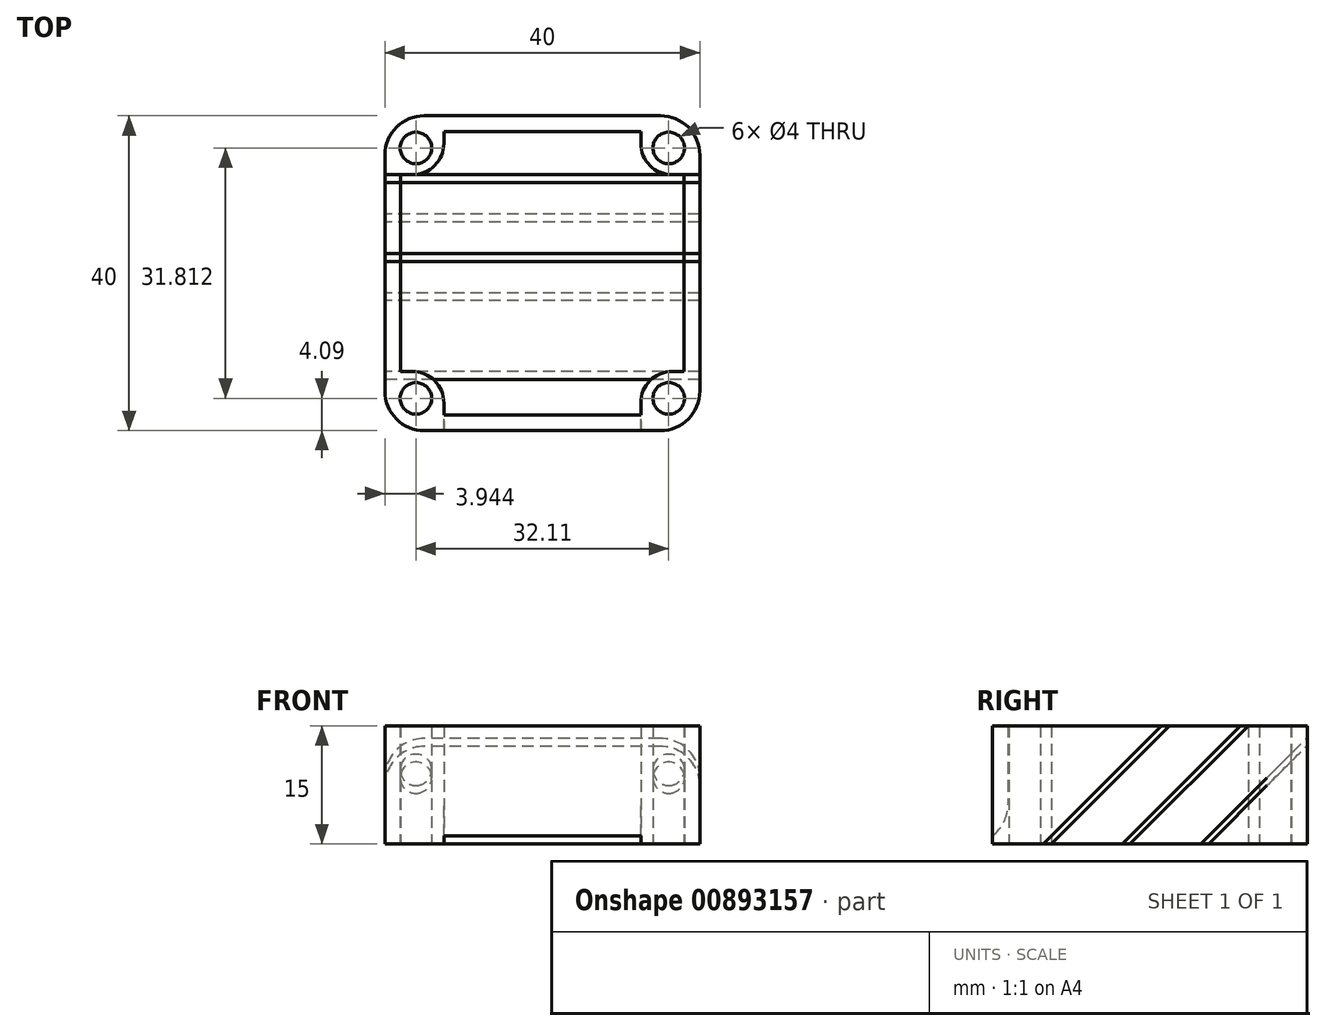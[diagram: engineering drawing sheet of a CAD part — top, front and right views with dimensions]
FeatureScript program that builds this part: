
annotation { "Feature Type Name" : "Feature", "Feature Type Description" : "" }
export const myFeature = defineFeature(function(context is Context, id is Id, definition is map)
    precondition{}
    {
        {
            var Q0;
            Q0=qCreatedBy(makeId("Top.planeOp"),FACE);
            var sketch = newSketch(context, id + "F0", { "sketchPlane" : qUnion([Q0])});
            skCircle(sketch, "E0", {"center": v(-57.98, 66.95) * mm, "radius": 2 * mm});
            skCircle(sketch, "E1", {"center": v(-25.87, 66.95) * mm, "radius": 2 * mm});
            skCircle(sketch, "E2", {"center": v(-25.87, 35.14) * mm, "radius": 2 * mm});
            skCircle(sketch, "E3", {"center": v(-57.98, 35.14) * mm, "radius": 2 * mm});
            skLineSegment(sketch, "E4.bottom", {"start": v(-21.92, 31.05) * mm, "end": v(-61.92, 31.05) * mm});
            skLineSegment(sketch, "E4.top", {"start": v(-21.92, 71.05) * mm, "end": v(-61.92, 71.05) * mm});
            skLineSegment(sketch, "E4.left", {"start": v(-21.92, 31.05) * mm, "end": v(-21.92, 71.05) * mm});
            skLineSegment(sketch, "E4.right", {"start": v(-61.92, 31.05) * mm, "end": v(-61.92, 71.05) * mm});
            skPoint(sketch, "E4.middle", {"position": v(-41.92, 51.05) * mm});
            skPoint(sketch, "E5", {"position": v(-61.92, 63.55) * mm});
            skPoint(sketch, "E6", {"position": v(-21.92, 63.55) * mm});
            skPoint(sketch, "E7", {"position": v(-61.92, 38.55) * mm});
            skPoint(sketch, "E8", {"position": v(-21.92, 38.55) * mm});
            skPoint(sketch, "E9", {"position": v(-54.42, 71.05) * mm});
            skPoint(sketch, "E10", {"position": v(-29.42, 71.05) * mm});
            skPoint(sketch, "E11", {"position": v(-29.42, 31.05) * mm});
            skPoint(sketch, "E12", {"position": v(-54.42, 31.05) * mm});
            skLineSegment(sketch, "E13", {"start": v(-61.92, 63.55) * mm, "end": v(-54.42, 63.55) * mm});
            skLineSegment(sketch, "E14", {"start": v(-54.42, 63.55) * mm, "end": v(-54.42, 71.05) * mm});
            skLineSegment(sketch, "E15", {"start": v(-29.42, 71.05) * mm, "end": v(-29.42, 63.55) * mm});
            skLineSegment(sketch, "E16", {"start": v(-29.42, 63.55) * mm, "end": v(-21.92, 63.55) * mm});
            skLineSegment(sketch, "E17", {"start": v(-61.92, 38.55) * mm, "end": v(-54.42, 38.55) * mm});
            skLineSegment(sketch, "E18", {"start": v(-54.42, 38.55) * mm, "end": v(-54.42, 31.05) * mm});
            skLineSegment(sketch, "E19", {"start": v(-21.92, 38.55) * mm, "end": v(-29.42, 38.55) * mm});
            skLineSegment(sketch, "E20", {"start": v(-29.42, 38.55) * mm, "end": v(-29.42, 31.05) * mm});
            skPoint(sketch, "E21", {"position": v(-59.92, 63.55) * mm});
            skPoint(sketch, "E22", {"position": v(-59.92, 38.55) * mm});
            skPoint(sketch, "E23", {"position": v(-54.42, 33.05) * mm});
            skPoint(sketch, "E24", {"position": v(-29.42, 33.05) * mm});
            skPoint(sketch, "E25", {"position": v(-23.92, 38.55) * mm});
            skPoint(sketch, "E26", {"position": v(-23.92, 63.55) * mm});
            skPoint(sketch, "E27", {"position": v(-29.42, 69.05) * mm});
            skPoint(sketch, "E28", {"position": v(-54.42, 69.05) * mm});
            skLineSegment(sketch, "E29", {"start": v(-59.92, 63.55) * mm, "end": v(-59.92, 38.55) * mm});
            skLineSegment(sketch, "E30", {"start": v(-54.42, 33.05) * mm, "end": v(-29.42, 33.05) * mm});
            skLineSegment(sketch, "E31", {"start": v(-23.92, 38.55) * mm, "end": v(-23.92, 63.55) * mm});
            skLineSegment(sketch, "E32", {"start": v(-29.42, 69.05) * mm, "end": v(-54.42, 69.05) * mm});
            skSolve(sketch);
        }
        {
            var Q0;
            Q0 = qSketchRegion(id + "F0", true);
            extrude(context, id + "F1", {"entities" : qUnion([Q0]), "depth" : 15 * mm, "offsetDistance" : 25 * mm});
        }
        {
            var Q0;
            Q0=makeQuery(id+"F1.opExtrude","SWEPT_EDGE",EDGE,{"disambiguationData":[OSD([sQuery(id+"F0.wireOp",EDGE,"E4.top"),sQuery(id+"F0.wireOp",EDGE,"E4.right")])]});
            var Q1;
            Q1=makeQuery(id+"F1.opExtrude","SWEPT_EDGE",EDGE,{"disambiguationData":[OSD([sQuery(id+"F0.wireOp",EDGE,"E4.bottom"),sQuery(id+"F0.wireOp",EDGE,"E4.right")])]});
            var Q2;
            Q2=makeQuery(id+"F1.opExtrude","SWEPT_EDGE",EDGE,{"disambiguationData":[OSD([sQuery(id+"F0.wireOp",EDGE,"E4.bottom"),sQuery(id+"F0.wireOp",EDGE,"E4.left")])]});
            var Q3;
            Q3=makeQuery(id+"F1.opExtrude","SWEPT_EDGE",EDGE,{"disambiguationData":[OSD([sQuery(id+"F0.wireOp",EDGE,"E4.top"),sQuery(id+"F0.wireOp",EDGE,"E4.left")])]});
            fillet(context, id + "F2", {"entities" : qUnion([Q0, Q1, Q2, Q3]), "radius" : 5 * mm, "tangentPropagation" : true, "allowEdgeOverflow" : false});
        }
        {
            var Q0;
            Q0=makeQuery(id+"F1.opExtrude","SWEPT_EDGE",EDGE,{"disambiguationData":[OSD([sQuery(id+"F0.wireOp",EDGE,"E13"),sQuery(id+"F0.wireOp",EDGE,"E14")])]});
            var Q1;
            Q1=makeQuery(id+"F1.opExtrude","SWEPT_EDGE",EDGE,{"disambiguationData":[OSD([sQuery(id+"F0.wireOp",EDGE,"E15"),sQuery(id+"F0.wireOp",EDGE,"E16")])]});
            var Q2;
            Q2=makeQuery(id+"F1.opExtrude","SWEPT_EDGE",EDGE,{"disambiguationData":[OSD([sQuery(id+"F0.wireOp",EDGE,"E19"),sQuery(id+"F0.wireOp",EDGE,"E20")])]});
            var Q3;
            Q3=makeQuery(id+"F1.opExtrude","SWEPT_EDGE",EDGE,{"disambiguationData":[OSD([sQuery(id+"F0.wireOp",EDGE,"E17"),sQuery(id+"F0.wireOp",EDGE,"E18")])]});
            fillet(context, id + "F3", {"entities" : qUnion([Q0, Q1, Q2, Q3]), "radius" : 4 * mm, "tangentPropagation" : true, "allowEdgeOverflow" : false});
        }
        {
            var Q0;
            Q0=makeQuery(id+"F1.opExtrude","SWEPT_FACE",FACE,{"disambiguationData":[OSD([sQuery(id+"F0.wireOp",EDGE,"E4.right")])]});
            var sketch = newSketch(context, id + "F4", { "sketchPlane" : qUnion([Q0])});
            skPoint(sketch, "E33", {"position": v(-66.05, 7.5) * mm});
            skPoint(sketch, "E34", {"position": v(-51.05, 0) * mm});
            skPoint(sketch, "E35", {"position": v(-58.55, 0) * mm});
            skPoint(sketch, "E36", {"position": v(-57.55, 0) * mm});
            skPoint(sketch, "E37", {"position": v(-66.05, 8.5) * mm});
            skLineSegment(sketch, "E38", {"start": v(-66.05, 7.5) * mm, "end": v(-58.55, 0) * mm});
            skLineSegment(sketch, "E39", {"start": v(-66.05, 8.5) * mm, "end": v(-57.55, 0) * mm});
            skLineSegment(sketch, "E40", {"start": v(-66.05, 7.5) * mm, "end": v(-66.05, 8.5) * mm});
            skLineSegment(sketch, "E41", {"start": v(-58.55, 0) * mm, "end": v(-57.55, 0) * mm});
            skLineSegment(sketch, "E42", {"start": v(-66.05, 8.5) * mm, "end": v(-66.05, 15) * mm});
            skLineSegment(sketch, "E43.1.0.0", {"start": v(-56.05, 7.5) * mm, "end": v(-48.55, 0) * mm});
            skLineSegment(sketch, "E43.1.0.1", {"start": v(-56.05, 8.5) * mm, "end": v(-47.55, 0) * mm});
            skLineSegment(sketch, "E43.1.0.2", {"start": v(-48.55, 0) * mm, "end": v(-47.55, 0) * mm});
            skLineSegment(sketch, "E43.2.0.0", {"start": v(-46.05, 7.5) * mm, "end": v(-38.55, 0) * mm});
            skLineSegment(sketch, "E43.2.0.1", {"start": v(-46.05, 8.5) * mm, "end": v(-37.55, 0) * mm});
            skLineSegment(sketch, "E43.2.0.2", {"start": v(-38.55, 0) * mm, "end": v(-37.55, 0) * mm});
            skLineSegment(sketch, "E43.direction1", {"start": v(-58.55, 0) * mm, "end": v(-48.55, 0) * mm, "construction": true});
            skLineSegment(sketch, "E44", {"start": v(-56.05, 7.5) * mm, "end": v(-63.55, 15) * mm});
            skLineSegment(sketch, "E45", {"start": v(-56.05, 8.5) * mm, "end": v(-62.55, 15) * mm});
            skLineSegment(sketch, "E46", {"start": v(-63.55, 15) * mm, "end": v(-62.55, 15) * mm});
            skLineSegment(sketch, "E47", {"start": v(-46.05, 7.5) * mm, "end": v(-53.55, 15) * mm});
            skLineSegment(sketch, "E48", {"start": v(-46.05, 8.5) * mm, "end": v(-52.55, 15) * mm});
            skLineSegment(sketch, "E49", {"start": v(-53.55, 15) * mm, "end": v(-52.55, 15) * mm});
            skLineSegment(sketch, "E50", {"start": v(-66.05, 7.5) * mm, "end": v(-70.94, 12.4) * mm});
            skLineSegment(sketch, "E51", {"start": v(-66.05, 8.5) * mm, "end": v(-70.94, 13.4) * mm});
            skLineSegment(sketch, "E52", {"start": v(-70.94, 13.4) * mm, "end": v(-70.94, 12.4) * mm});
            skLineSegment(sketch, "E53", {"start": v(-70.94, 13.4) * mm, "end": v(-66.05, 8.5) * mm});
            skLineSegment(sketch, "E54", {"start": v(-70.94, 12.4) * mm, "end": v(-66.05, 7.5) * mm});
            skSolve(sketch);
        }
        {
            var Q0;
            Q0 = qSketchRegion(id + "F4", true);
            extrude(context, id + "F5", {"entities" : qUnion([Q0]), "oppositeDirection" : true, "depth" : 40 * mm, "offsetDistance" : 25 * mm});
        }
        {
            var Q0;
            Q0=makeQuery(id+"F5.opExtrude","CAP_EDGE",EDGE,{"disambiguationData":[OSD([sQuery(id+"F4.wireOp",EDGE,"E52")])],"isStart":true});
            var Q1;
            Q1=makeQuery(id+"F5.opExtrude","CAP_EDGE",EDGE,{"disambiguationData":[OSD([sQuery(id+"F4.wireOp",EDGE,"E52")])],"isStart":false});
            fillet(context, id + "F6", {"entities" : qUnion([Q0, Q1]), "radius" : 5 * mm, "tangentPropagation" : true, "allowEdgeOverflow" : false});
        }
        {
            var Q0;
            Q0=makeQuery(id+"F1.opExtrude","CAP_FACE",FACE,{"disambiguationData":[OSD([sQuery(id+"F0.wireOp",EDGE,"E0"),sQuery(id+"F0.wireOp",EDGE,"E1"),sQuery(id+"F0.wireOp",EDGE,"E2"),sQuery(id+"F0.wireOp",EDGE,"E3"),sQuery(id+"F0.wireOp",EDGE,"E4.bottom"),sQuery(id+"F0.wireOp",EDGE,"E4.top"),sQuery(id+"F0.wireOp",EDGE,"E4.left"),sQuery(id+"F0.wireOp",EDGE,"E4.right"),sQuery(id+"F0.wireOp",EDGE,"E13"),sQuery(id+"F0.wireOp",EDGE,"E14"),sQuery(id+"F0.wireOp",EDGE,"E15"),sQuery(id+"F0.wireOp",EDGE,"E16"),sQuery(id+"F0.wireOp",EDGE,"E17"),sQuery(id+"F0.wireOp",EDGE,"E18"),sQuery(id+"F0.wireOp",EDGE,"E19"),sQuery(id+"F0.wireOp",EDGE,"E20"),sQuery(id+"F0.wireOp",EDGE,"E29"),sQuery(id+"F0.wireOp",EDGE,"E30"),sQuery(id+"F0.wireOp",EDGE,"E31"),sQuery(id+"F0.wireOp",EDGE,"E32")])],"isStart":true});
            var sketch = newSketch(context, id + "F7", { "sketchPlane" : qUnion([Q0])});
            skCircle(sketch, "E55", {"center": v(-25.87, -66.95) * mm, "radius": 2 * mm});
            skCircle(sketch, "E56", {"center": v(-57.98, -66.95) * mm, "radius": 2 * mm});
            skSolve(sketch);
        }
        {
            var Q0;
            Q0 = qSketchRegion(id + "F7", true);
            extrude(context, id + "F8", {"entities" : qUnion([Q0]), "operationType" : NewBodyOperationType.REMOVE, "oppositeDirection" : true, "depth" : 25 * mm, "offsetDistance" : 25 * mm});
        }
        {
            var Q0;
            Q0=makeQuery(id+"F1.opExtrude","CAP_EDGE",EDGE,{"disambiguationData":[OSD([sQuery(id+"F0.wireOp",EDGE,"E30")])],"isStart":true});
            fillet(context, id + "F9", {"entities" : qUnion([Q0]), "radius" : 5 * mm, "tangentPropagation" : true, "allowEdgeOverflow" : false});
        }
    });
